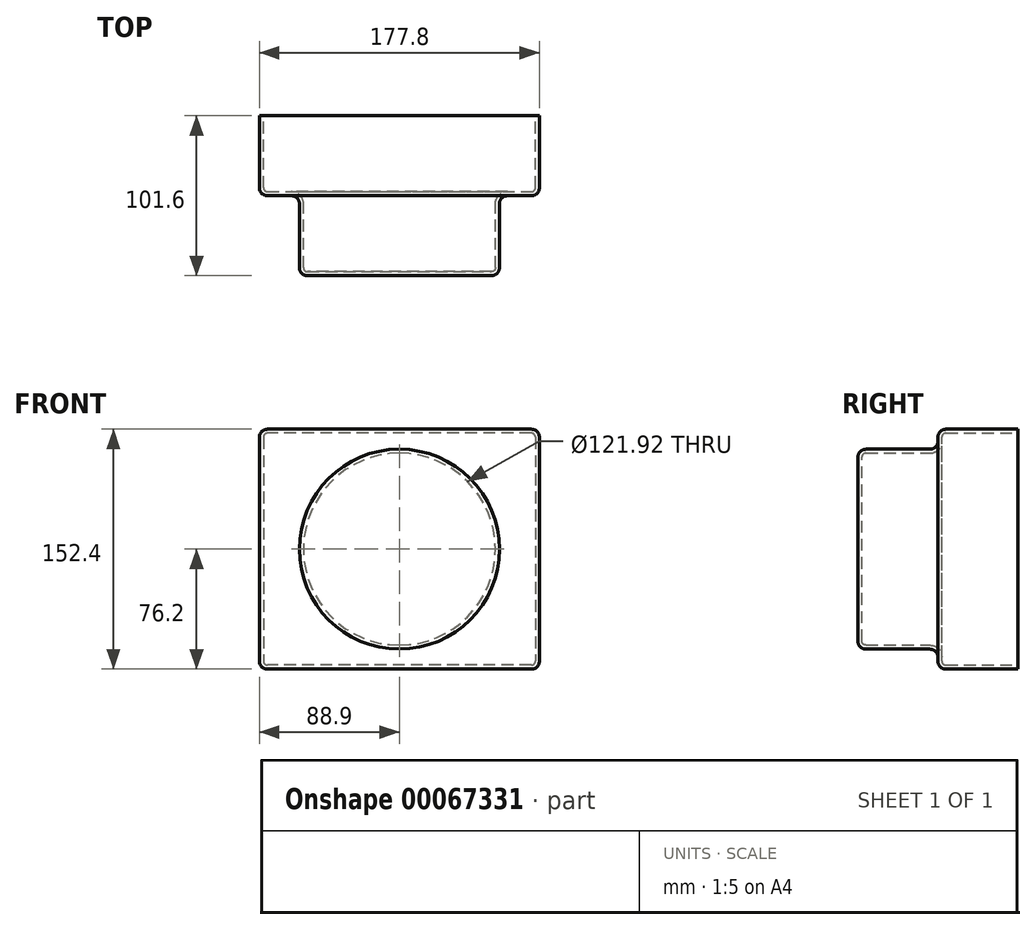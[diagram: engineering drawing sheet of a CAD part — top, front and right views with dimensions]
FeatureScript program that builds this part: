
annotation { "Feature Type Name" : "Feature", "Feature Type Description" : "" }
export const myFeature = defineFeature(function(context is Context, id is Id, definition is map)
    precondition{}
    {
        {
            var Q0;
            Q0=qCreatedBy(makeId("Front.planeOp"),FACE);
            var sketch = newSketch(context, id + "F0", { "sketchPlane" : qUnion([Q0])});
            skLineSegment(sketch, "E0.rect.bottom", {"start": v(88.9, 76.2) * mm, "end": v(-88.9, 76.2) * mm});
            skLineSegment(sketch, "E0.rect.top", {"start": v(88.9, -76.2) * mm, "end": v(-88.9, -76.2) * mm});
            skLineSegment(sketch, "E0.rect.left", {"start": v(88.9, 76.2) * mm, "end": v(88.9, -76.2) * mm});
            skLineSegment(sketch, "E0.rect.right", {"start": v(-88.9, 76.2) * mm, "end": v(-88.9, -76.2) * mm});
            skPoint(sketch, "E0.rect.middle", {"position": v(0, 0) * mm});
            skSolve(sketch);
        }
        {
            var Q0;
            Q0 = qSketchRegion(id + "F0", true);
            extrude(context, id + "F1", {"entities" : qUnion([Q0]), "depth" : 50.8 * mm});
        }
        {
            var Q0;
            Q0=makeQuery(id+"F1.opExtrude","CAP_FACE",FACE,{"disambiguationData":[OSD([sQuery(id+"F0.wireOp",EDGE,"E0.rect.bottom"),sQuery(id+"F0.wireOp",EDGE,"E0.rect.top"),sQuery(id+"F0.wireOp",EDGE,"E0.rect.left"),sQuery(id+"F0.wireOp",EDGE,"E0.rect.right")])],"isStart":false});
            var sketch = newSketch(context, id + "F2", { "sketchPlane" : qUnion([Q0])});
            skCircle(sketch, "E1", {"center": v(0, 0) * mm, "radius": 63.5 * mm});
            skSolve(sketch);
        }
        {
            var Q0;
            Q0=makeQuery(id+"F2.imprint","IMPRINT",FACE,{"disambiguationData":[TD([[makeQuery(id+"F2.imprint","IMPRINT",EDGE,{"derivedFrom":sQuery(id+"F2.wireOp",EDGE,"E1")}),1.0]])]});
            extrude(context, id + "F3", {"entities" : qUnion([Q0]), "operationType" : NewBodyOperationType.ADD, "depth" : 50.8 * mm});
        }
        {
            var Q0;
            Q0=makeQuery(id+"F3.opExtrude","CAP_EDGE",EDGE,{"disambiguationData":[OSD([sQuery(id+"F2.wireOp",EDGE,"E1")])],"isStart":false});
            var Q1;
            Q1=makeQuery(id+"F3.opExtrude","CAP_EDGE",EDGE,{"disambiguationData":[OSD([sQuery(id+"F2.wireOp",EDGE,"E1")])],"isStart":true});
            var Q2;
            Q2=makeQuery(id+"F1.opExtrude","CAP_FACE",FACE,{"disambiguationData":[OSD([sQuery(id+"F0.wireOp",EDGE,"E0.rect.bottom"),sQuery(id+"F0.wireOp",EDGE,"E0.rect.top"),sQuery(id+"F0.wireOp",EDGE,"E0.rect.left"),sQuery(id+"F0.wireOp",EDGE,"E0.rect.right")])],"isStart":false});
            var Q3;
            Q3=makeQuery(id+"F1.opExtrude","SWEPT_EDGE",EDGE,{"disambiguationData":[OSD([sQuery(id+"F0.wireOp",EDGE,"E0.rect.bottom"),sQuery(id+"F0.wireOp",EDGE,"E0.rect.left")])]});
            var Q4;
            Q4=makeQuery(id+"F1.opExtrude","SWEPT_EDGE",EDGE,{"disambiguationData":[OSD([sQuery(id+"F0.wireOp",EDGE,"E0.rect.bottom"),sQuery(id+"F0.wireOp",EDGE,"E0.rect.right")])]});
            var Q5;
            Q5=makeQuery(id+"F1.opExtrude","SWEPT_EDGE",EDGE,{"disambiguationData":[OSD([sQuery(id+"F0.wireOp",EDGE,"E0.rect.top"),sQuery(id+"F0.wireOp",EDGE,"E0.rect.right")])]});
            var Q6;
            Q6=makeQuery(id+"F1.opExtrude","SWEPT_EDGE",EDGE,{"disambiguationData":[OSD([sQuery(id+"F0.wireOp",EDGE,"E0.rect.top"),sQuery(id+"F0.wireOp",EDGE,"E0.rect.left")])]});
            fillet(context, id + "F4", {"entities" : qUnion([Q0, Q1, Q2, Q3, Q4, Q5, Q6]), "radius" : 5.08 * mm, "tangentPropagation" : true, "allowEdgeOverflow" : false});
        }
        {
            var Q0;
            Q0=makeQuery(id+"F1.opExtrude","CAP_FACE",FACE,{"disambiguationData":[OSD([sQuery(id+"F0.wireOp",EDGE,"E0.rect.bottom"),sQuery(id+"F0.wireOp",EDGE,"E0.rect.top"),sQuery(id+"F0.wireOp",EDGE,"E0.rect.left"),sQuery(id+"F0.wireOp",EDGE,"E0.rect.right")])],"isStart":true});
            shell(context, id + "F5", {"entities" : qUnion([Q0]), "thickness" : 2.54 * mm});
        }
    });
